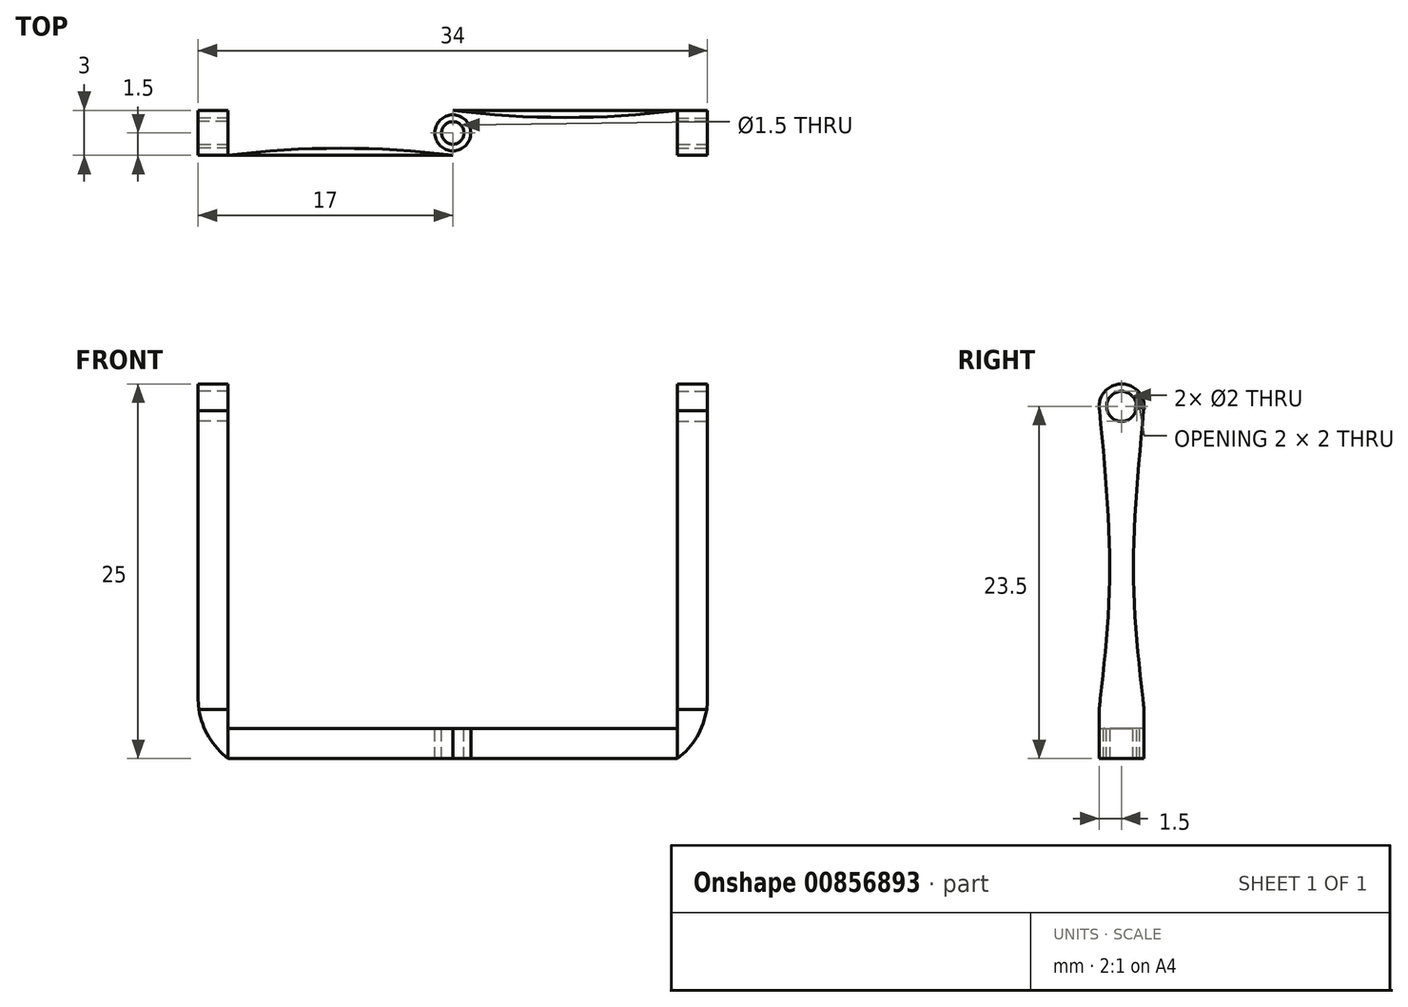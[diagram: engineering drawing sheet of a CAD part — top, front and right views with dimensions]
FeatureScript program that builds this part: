
annotation { "Feature Type Name" : "Feature", "Feature Type Description" : "" }
export const myFeature = defineFeature(function(context is Context, id is Id, definition is map)
    precondition{}
    {
        {
            var Q0;
            Q0=qCreatedBy(makeId("Front.planeOp"),FACE);
            var sketch = newSketch(context, id + "F0", { "sketchPlane" : qUnion([Q0])});
            skLineSegment(sketch, "E0", {"start": v(0, 2) * mm, "end": v(15, 2) * mm});
            skLineSegment(sketch, "E1", {"start": v(15, 2) * mm, "end": v(15, 25) * mm});
            skLineSegment(sketch, "E2", {"start": v(15, 25) * mm, "end": v(17, 25) * mm});
            skLineSegment(sketch, "E3", {"start": v(17, 25) * mm, "end": v(17, 0) * mm});
            skLineSegment(sketch, "E4", {"start": v(17, 0) * mm, "end": v(0, 0) * mm});
            skLineSegment(sketch, "E5", {"start": v(0, 0) * mm, "end": v(0, 2) * mm});
            skSolve(sketch);
        }
        {
            var Q0;
            Q0=makeQuery(id+"F0.imprint","IMPRINT",FACE,{"disambiguationData":[TD([[makeQuery(id+"F0.imprint","IMPRINT",EDGE,{"derivedFrom":sQuery(id+"F0.wireOp",EDGE,"E0")}),-1.0]])]});
            extrude(context, id + "F1", {"entities" : qUnion([Q0]), "endBound" : BoundingType.SYMMETRIC, "depth" : 3 * mm, "offsetDistance" : 25 * mm});
        }
        {
            var Q0;
            Q0=makeQuery(id+"F1.opExtrude","SWEPT_FACE",FACE,{"disambiguationData":[OSD([sQuery(id+"F0.wireOp",EDGE,"E3")])]});
            var sketch = newSketch(context, id + "F2", { "sketchPlane" : qUnion([Q0])});
            skCircle(sketch, "E6", {"center": v(0, 23.5) * mm, "radius": 1 * mm});
            skSolve(sketch);
        }
        {
            var Q0;
            Q0=makeQuery(id+"F2.imprint","IMPRINT",FACE,{"disambiguationData":[TD([[makeQuery(id+"F2.imprint","IMPRINT",EDGE,{"derivedFrom":sQuery(id+"F2.wireOp",EDGE,"E6")}),1.0]])]});
            extrude(context, id + "F3", {"entities" : qUnion([Q0]), "operationType" : NewBodyOperationType.REMOVE, "endBound" : BoundingType.THROUGH_ALL, "oppositeDirection" : true, "depth" : 25 * mm, "offsetDistance" : 25 * mm});
        }
        {
            var Q0;
            Q0=makeQuery(id+"F1.opExtrude","SWEPT_FACE",FACE,{"disambiguationData":[OSD([sQuery(id+"F0.wireOp",EDGE,"E3")])]});
            var sketch = newSketch(context, id + "F4", { "sketchPlane" : qUnion([Q0])});
            skCircle(sketch, "E7", {"center": v(0, 23.5) * mm, "radius": 1.5 * mm});
            skFitSpline(sketch, "E8", {"points": [v(-1.5, 23.5) * mm, v(-0.8, 12.47) * mm, v(-1.5, 3.26) * mm], "startDerivative": vector(2.08, -21.6) * mm, "endDerivative": vector(-2.14, -18.84) * mm});
            skFitSpline(sketch, "E9.MirrorCS", {"points": [v(1.5, 23.5) * mm, v(0.8, 12.47) * mm, v(1.5, 3.26) * mm], "startDerivative": vector(-2.08, -21.6) * mm, "endDerivative": vector(2.14, -18.84) * mm});
            skLineSegment(sketch, "E10", {"start": v(-1.5, 23.5) * mm, "end": v(-1.5, 3.26) * mm});
            skLineSegment(sketch, "E11", {"start": v(1.5, 23.5) * mm, "end": v(1.5, 3.26) * mm});
            skSolve(sketch);
        }
        {
            var Q0;
            {var subQ0=sQuery(id+"F4.wireOp",EDGE,"E10");Q0=makeQuery(id+"F4.imprint","IMPRINT",FACE,{"disambiguationData":[TD([[makeQuery(id+"F4.imprint","IMPRINT",EDGE,{"derivedFrom":subQ0}),1.0]])]});}
            var Q1;
            {var subQ0=sQuery(id+"F4.wireOp",EDGE,"E11");Q1=makeQuery(id+"F4.imprint","IMPRINT",FACE,{"disambiguationData":[TD([[makeQuery(id+"F4.imprint","IMPRINT",EDGE,{"derivedFrom":subQ0}),-1.0]])]});}
            extrude(context, id + "F5", {"entities" : qUnion([Q0, Q1]), "operationType" : NewBodyOperationType.REMOVE, "endBound" : BoundingType.THROUGH_ALL, "oppositeDirection" : true, "depth" : 25 * mm, "offsetDistance" : 25 * mm});
        }
        {
            var Q0;
            Q0=makeQuery(id+"F1.opExtrude","SWEPT_FACE",FACE,{"disambiguationData":[OSD([sQuery(id+"F0.wireOp",EDGE,"E3")])]});
            var sketch = newSketch(context, id + "F6", { "sketchPlane" : qUnion([Q0])});
            skCircle(sketch, "E12", {"center": v(0, 23.5) * mm, "radius": 1.5 * mm});
            skLineSegment(sketch, "E13", {"start": v(0, 25) * mm, "end": v(-1.5, 25) * mm});
            skLineSegment(sketch, "E14", {"start": v(-1.5, 25) * mm, "end": v(-1.5, 23.5) * mm});
            skLineSegment(sketch, "E15", {"start": v(0, 25) * mm, "end": v(1.5, 25) * mm});
            skLineSegment(sketch, "E16", {"start": v(1.5, 25) * mm, "end": v(1.5, 23.5) * mm});
            skSolve(sketch);
        }
        {
            var Q0;
            {var subQ2=sQuery(id+"F6.wireOp",EDGE,"E13");Q0=makeQuery(id+"F6.imprint","IMPRINT",FACE,{"disambiguationData":[TD([[makeQuery(id+"F6.imprint","IMPRINT",EDGE,{"derivedFrom":subQ2}),-1.0]])]});}
            var Q1;
            {var subQ2=sQuery(id+"F6.wireOp",EDGE,"E15");Q1=makeQuery(id+"F6.imprint","IMPRINT",FACE,{"disambiguationData":[TD([[makeQuery(id+"F6.imprint","IMPRINT",EDGE,{"derivedFrom":subQ2}),-1.0]])]});}
            extrude(context, id + "F7", {"entities" : qUnion([Q0, Q1]), "operationType" : NewBodyOperationType.REMOVE, "endBound" : BoundingType.THROUGH_ALL, "oppositeDirection" : true, "depth" : 25 * mm, "offsetDistance" : 25 * mm});
        }
        {
            var Q0;
            Q0=makeQuery(id+"F1.opExtrude","SWEPT_BODY",BODY,{"disambiguationData":[OSD([sQuery(id+"F0.wireOp",EDGE,"E0"),sQuery(id+"F0.wireOp",EDGE,"E1"),sQuery(id+"F0.wireOp",EDGE,"E2"),sQuery(id+"F0.wireOp",EDGE,"E3"),sQuery(id+"F0.wireOp",EDGE,"E4"),sQuery(id+"F0.wireOp",EDGE,"E5")])]});
            var Q1;
            Q1=qCreatedBy(makeId("Right.planeOp"),FACE);
            mirror(context, id + "F8", {"operationType" : NewBodyOperationType.ADD, "entities" : qUnion([Q0]), "mirrorPlane" : qUnion([Q1])});
        }
        {
            var Q0;
            {var subQ0=makeQuery(id+"F1.opExtrude","SWEPT_FACE",FACE,{"disambiguationData":[OSD([sQuery(id+"F0.wireOp",EDGE,"E0")])]});Q0=makeQuery(id+"F8.boolean.opBoolean","MERGE",FACE,{"derivedFrom":[subQ0,makeQuery(id+"F8.opPattern","COPY",FACE,{"derivedFrom":subQ0,"instanceName":"1"})]});}
            var sketch = newSketch(context, id + "F9", { "sketchPlane" : qUnion([Q0])});
            skCircle(sketch, "E17", {"center": v(0, 0) * mm, "radius": 0.75 * mm});
            skSolve(sketch);
        }
        {
            var Q0;
            Q0=makeQuery(id+"F9.imprint","IMPRINT",FACE,{"disambiguationData":[TD([[makeQuery(id+"F9.imprint","IMPRINT",EDGE,{"derivedFrom":sQuery(id+"F9.wireOp",EDGE,"E17")}),1.0]])]});
            extrude(context, id + "F10", {"entities" : qUnion([Q0]), "operationType" : NewBodyOperationType.REMOVE, "endBound" : BoundingType.THROUGH_ALL, "oppositeDirection" : true, "depth" : 25 * mm, "offsetDistance" : 25 * mm});
        }
        {
            var Q0;
            {var subQ0=makeQuery(id+"F1.opExtrude","SWEPT_FACE",FACE,{"disambiguationData":[OSD([sQuery(id+"F0.wireOp",EDGE,"E0")])]});Q0=makeQuery(id+"F8.boolean.opBoolean","MERGE",FACE,{"derivedFrom":[subQ0,makeQuery(id+"F8.opPattern","COPY",FACE,{"derivedFrom":subQ0,"instanceName":"1"})]});}
            var sketch = newSketch(context, id + "F11", { "sketchPlane" : qUnion([Q0])});
            skCircle(sketch, "E18", {"center": v(0, 0) * mm, "radius": 1.2 * mm});
            skArc(sketch, "E19", {"start": v(-15, 1.5) * mm, "mid": v(-7.5, 1.03) * mm, "end": v(0, 1.5) * mm});
            skArc(sketch, "E20.MirrorCS", {"start": v(-15, -1.5) * mm, "mid": v(-7.5, -1.03) * mm, "end": v(0, -1.5) * mm});
            skArc(sketch, "E21.MirrorCS", {"start": v(15, 1.5) * mm, "mid": v(7.5, 1.03) * mm, "end": v(0, 1.5) * mm});
            skArc(sketch, "E22.MirrorCS", {"start": v(15, -1.5) * mm, "mid": v(7.5, -1.03) * mm, "end": v(0, -1.5) * mm});
            skLineSegment(sketch, "E23", {"start": v(-15, 1.5) * mm, "end": v(15, 1.5) * mm});
            skLineSegment(sketch, "E24", {"start": v(15, -1.5) * mm, "end": v(-15, -1.5) * mm});
            skSolve(sketch);
        }
        {
            var Q0;
            {var subQ0=sQuery(id+"F11.wireOp",EDGE,"E19");Q0=makeQuery(id+"F11.imprint","IMPRINT",FACE,{"disambiguationData":[TD([[makeQuery(id+"F11.imprint","IMPRINT",EDGE,{"derivedFrom":subQ0}),1.0]])]});}
            var Q1;
            {var subQ0=sQuery(id+"F11.wireOp",EDGE,"E21.MirrorCS");Q1=makeQuery(id+"F11.imprint","IMPRINT",FACE,{"disambiguationData":[TD([[makeQuery(id+"F11.imprint","IMPRINT",EDGE,{"derivedFrom":subQ0}),-1.0]])]});}
            var Q2;
            {var subQ0=sQuery(id+"F11.wireOp",EDGE,"E22.MirrorCS");Q2=makeQuery(id+"F11.imprint","IMPRINT",FACE,{"disambiguationData":[TD([[makeQuery(id+"F11.imprint","IMPRINT",EDGE,{"derivedFrom":subQ0}),1.0]])]});}
            var Q3;
            {var subQ0=sQuery(id+"F11.wireOp",EDGE,"E20.MirrorCS");Q3=makeQuery(id+"F11.imprint","IMPRINT",FACE,{"disambiguationData":[TD([[makeQuery(id+"F11.imprint","IMPRINT",EDGE,{"derivedFrom":subQ0}),-1.0]])]});}
            extrude(context, id + "F12", {"entities" : qUnion([Q0, Q1, Q2, Q3]), "operationType" : NewBodyOperationType.REMOVE, "endBound" : BoundingType.THROUGH_ALL, "oppositeDirection" : true, "depth" : 25 * mm, "offsetDistance" : 25 * mm});
        }
        {
            var Q0;
            Q0=makeQuery(id+"F8.opPattern","COPY",EDGE,{"derivedFrom":makeQuery(id+"F1.opExtrude","SWEPT_EDGE",EDGE,{"disambiguationData":[OSD([sQuery(id+"F0.wireOp",EDGE,"E0"),sQuery(id+"F0.wireOp",EDGE,"E1")])]}),"instanceName":"1"});
            var Q1;
            Q1=makeQuery(id+"F8.opPattern","COPY",EDGE,{"derivedFrom":makeQuery(id+"F1.opExtrude","SWEPT_EDGE",EDGE,{"disambiguationData":[OSD([sQuery(id+"F0.wireOp",EDGE,"E3"),sQuery(id+"F0.wireOp",EDGE,"E4")])]}),"instanceName":"1"});
            var Q2;
            Q2=makeQuery(id+"F1.opExtrude","SWEPT_EDGE",EDGE,{"disambiguationData":[OSD([sQuery(id+"F0.wireOp",EDGE,"E0"),sQuery(id+"F0.wireOp",EDGE,"E1")])]});
            var Q3;
            Q3=makeQuery(id+"F1.opExtrude","SWEPT_EDGE",EDGE,{"disambiguationData":[OSD([sQuery(id+"F0.wireOp",EDGE,"E3"),sQuery(id+"F0.wireOp",EDGE,"E4")])]});
            fillet(context, id + "F13", {"entities" : qUnion([Q0, Q1, Q2, Q3]), "radius" : 5 * mm, "tangentPropagation" : true, "allowEdgeOverflow" : false});
        }
    });
